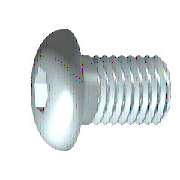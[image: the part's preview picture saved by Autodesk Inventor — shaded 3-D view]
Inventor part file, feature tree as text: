
AUTODESK INVENTOR PART (.ipt)
format: ipt  version: 2015 (Build 190159000, 159)  size: 193,536 bytes
history: native  units: mm (DEFAULTED — no unit token found)
features: sketch x2, extrude x1, plane x1, fillet x1
ambient origin geometry x7: Origin, YZ Plane, XY Plane, X Axis, Y Axis, Z Axis, Center Point
bodies: Solid1 (feature_tree), Body (feature_tree)
feature tree (5):
  extrude  "Slot"  Depth=1.8542mm
  plane  "Work Plane1"
  fillet  "Fillet2"  Radius=1.8542mm
  sketch  "Sketch1"  dims[d1=11.10976mm d2=1.59014mm d3=1.8542mm]
  sketch  "Sketch2"  dims[d4=1.1176mm d5=60.0deg d6=3.5052mm d7=3.5052mm d8=2.287693mm d9=6.6548mm d10=90.0deg d11=10.0mm d12=0.0mm d13=11.10976mm d14=0.0mm d15=0.486918mm d16=0.486918mm d17=1.6002mm d19=0.0mm d26=12.7mm d27=45.0deg d28=0.0mm d29=0.0mm d30=0.1mm]
